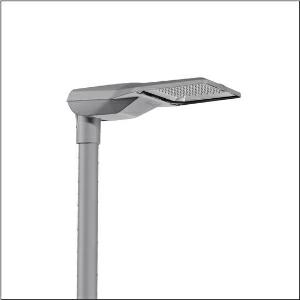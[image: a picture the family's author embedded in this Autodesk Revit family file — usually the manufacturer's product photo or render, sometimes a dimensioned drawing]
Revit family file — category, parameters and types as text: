
# Revit family: streetlight_sl_21_iq_midi___st0_8a_5xe3c31g08mb_0ba1
name_source: partatom
category: Lighting Fixtures
units: mm (PartAtom-declared; Revit-internal decimal feet)

## family parameters
Cut with Voids When Loaded = No
Host = Face
Light Source = No
Part Type = Normal
Room Calculation Point = No
Round Connector Dimension = Use Diameter
Shared = No

## types (1)
- --- (1 x LED, 19500 lm, 146.7 W, 3000K)
    Apparent Load = 147 VA
    CIE Flux Codes = 38 75 97 100 100
    Color Rendering = 70
    Color Temperature = 3000K
    Default Elevation = 1800 mm
    Description = Streetlight SL 21 iQ midi, mast luminaire, primary light control with lens, of PMMA, primary optical cover: cover, of toughened safety glass, transparent, light distribution: ST0.8a, light emission: direct distribution, primary light characteristic: asymmetric, installation type: post-top, side-entry, LED, High Power LED, rated luminous flux: 19.500lm, luminous efficacy: 133lm/W, light colour: 730, colour temperature: 3000K, control: Street-Remote, Auto-Match, Temp-Guard, Lumen-Switch, Night-Set, Smart-Wire, Light-Fading, Desk-Remote (wireless, voltage-free reading and setting of iQ features in the workshop via application-optimized NFC function/RFID function), optimised constant luminous flux control (CLO 2.0), presetting dimming linear, mains connection: 230..240V, AC, 50/60Hz, start of lifetime: 147W, end of service life: 161W, reduction: 62W, luminaire housing, of diecast aluminium, powder-coated, Siteco® metallic grey (DB 702S), corrosivity category C5 mid according to DIN EN ISO 12944, please order mast flange separately, inclination adjustable: 0°, 5°, 10°, 15°, sealing non-destructively replaceable, multi-level sealing system, length: 644mm, width: 335mm, height: 110mm, mast flange for spigot size: 42mm (side-entry): 5XC10008XM4, 60/48mm (side-entry/post-top): 5XC10108XM2, 76/60mm (side-entry/post-top): 5XC10108XM1, protection rating (complete): IP66, insulation class (complete): insulation class II (safety insulation), certification: CE, ENEC, ENEC+, VDE, impact resistance: IK09, permissible operating ambient temperature for outdoor applications: -40..+50°C, standard-compliant lighting for roads and squares, packaging unit: 1 piece

Light Distribution: ST0.8a
    Height = 111 mm
    Lamp = 1 x LED
    Lamp Light Flux = 19500 lm
    Lamp Power = 146.7 W
    Lamp count = 1
    Length = 644 mm
    Luminous efficacy = 133 lm/W
    Manufacturer = Siteco
    ModVariant = No
    Model = 5XE3C31G08MB
    Number of Poles = 1
    OnlyDefault = Yes
    Power Factor = 1
    Product Name = Streetlight SL 21 iQ midi | ST0.8a
    Product group = mast luminaire | pylon top
    ProductGroupID = 6100
    Protection Class = Protection class II
    Protection Degree = IP 66
    RLX_Detail_Level = 1
    RLX_Emergency_Light_Flux = 0 lm
    RLX_Emergency_Type = 0
    RLX_Emergency_Type_DB = No
    RlxData = <blob elided: 90837 chars, md5=7b15ed6d>
    Socket = socket
    Standby Power = 0 W
    System Light Flux = 19499 lm
    System Power = 147 W
    Type Comments = factory setting: luminous flux: 100 % | dim-lin: 254 | 753 mA
    Type Image = l_1004298.jpg
    URL = http://relux.com
    VarID = @adj_119717
    Voltage = 0 V
    Weight = 0.00 kg
    Width = 336 mm

## geometry (parser evidence)
native form markers: Blend x4, Sweep x11
no freeform markers — native parametric forms only
